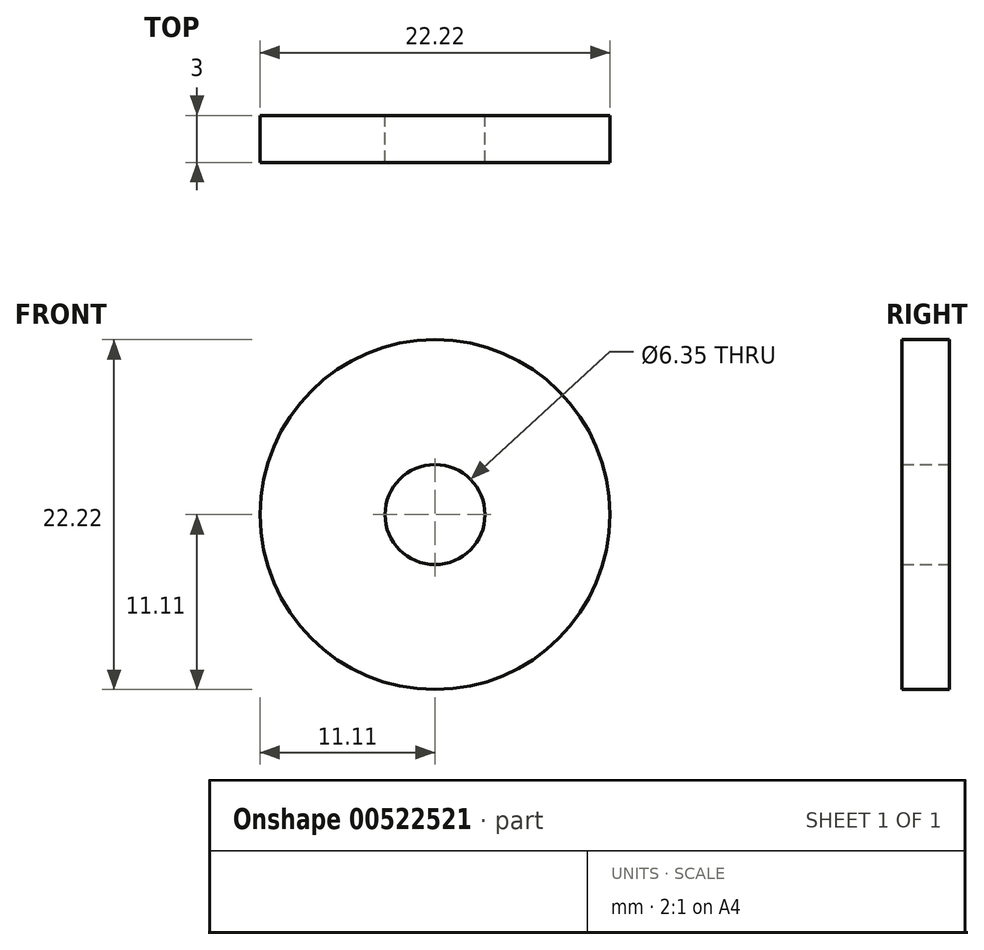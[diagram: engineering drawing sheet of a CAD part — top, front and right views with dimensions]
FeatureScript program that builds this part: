
annotation { "Feature Type Name" : "Feature", "Feature Type Description" : "" }
export const myFeature = defineFeature(function(context is Context, id is Id, definition is map)
    precondition{}
    {
        {
            assignVariable(context, id + "F0", {"name" : "thickness", "minmax" : VariableMinMaxSelection.MINIMUM, "extendEntities" : false, "measureFromAxis" : false, "distance" : 0 * mm, "xOffset" : 0 * mm, "yOffset" : 0 * mm, "zOffset" : 0 * mm, "componentSelector" : AxisWithCustom.DISTANCE, "customOffset" : 0 * mm, "radius" : false, "description" : "", "measurementMode" : VariableMeasurementMode.DISTANCE, "anyValue" : 3, "mode" : VariableMode.ASSIGNED});
        }
        {
            var Q0;
            Q0=qCreatedBy(makeId("Front.planeOp"),FACE);
            var sketch = newSketch(context, id + "F1", { "sketchPlane" : qUnion([Q0]), "disableImprinting" : false});
            skCircle(sketch, "E0", {"center": v(0, 0) * mm, "radius": 3.18 * mm});
            skCircle(sketch, "E1", {"center": v(0, 0) * mm, "radius": 11.11 * mm});
            skSolve(sketch);
        }
        {
            var Q0;
            Q0=makeQuery(id+"F1.imprint","IMPRINT",FACE,{"disambiguationData":[TD([[makeQuery(id+"F1.imprint","IMPRINT",EDGE,{"derivedFrom":sQuery(id+"F1.wireOp",EDGE,"E0")}),-1.0]])]});
            extrude(context, id + "F2", {"entities" : qUnion([Q0]), "depth" : (getVariable(context, 'thickness')) * mm, "offsetDistance" : 25 * mm});
        }
    });
